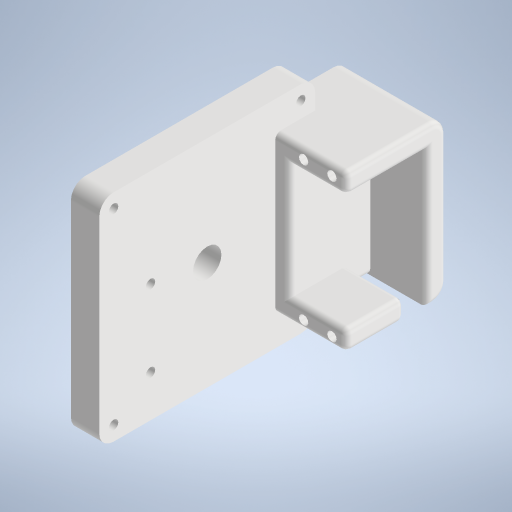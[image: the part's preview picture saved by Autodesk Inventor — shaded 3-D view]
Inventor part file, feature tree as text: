
AUTODESK INVENTOR PART (.ipt)
format: ipt  version: 2023 (Build 270158000, 158)  size: 377,344 bytes
history: native  units: in
note: dims shown in document units (in); Inventor stores cm internally (conversion verified against a paired STEP export)
features: extrude x9, sketch x7, fillet x5
ambient origin geometry x8: Origin, YZ Plane, XZ Plane, XY Plane, X Axis, Y Axis, Z Axis, Center Point
bodies: Solid1 (feature_tree)
feature tree (21):
  extrude  "Extrusion1"  Depth=2.1654in
  sketch  "Sketch2"  dims[d9=0.3937in d10=0.0in d11=0.2756in]
  extrude  "Extrusion2"  Depth=0.2756in
  extrude  "Extrusion3"  Depth=0.2756in
  extrude  "Extrusion5"  Depth=0.2756in
  extrude  "Extrusion6"  Depth=0.1969in TaperAngle=0.0deg
  fillet  "Fillet2"  Radius=0.1969in
  sketch  "Sketch8"  dims[d16=0.9843in d17=0.0in d18=0.1969in d19=0.0in d25=0.1969in d26=0.0in]
  extrude  "Extrusion8"  Depth=0.1969in
  extrude  "Extrusion9"  Depth=0.1969in
  fillet  "Fillet3"  Radius=0.1575in
  fillet  "Fillet4"  Radius=0.3937in
  fillet  "Fillet5"  Radius=0.3937in
  extrude  "Extrusion10"  Depth=0.1969in
  extrude  "Extrusion11"  Depth=0.1969in
  fillet  "Fillet6"  Radius=0.3937in
  sketch  "Sketch1"  dims[d0=3.3268in d1=2.1654in]
  sketch  "Sketch4"  dims[d12=1.122in d13=0.2756in]
  sketch  "Sketch5"  dims[d14=1.122in d15=0.2756in]
  sketch  "Sketch9"  dims[d27=0.315in d29=0.1969in]
  sketch  "Sketch10"  dims[d30=0.1575in d31=0.1299in d32=0.1575in d34=0.3937in d35=0.3937in d36=0.0in d54=0.1969in d55=0.8268in d56=0.3937in d57=0.0787in d58=0.0in d59=0.0in d60=0.0in d61=0.0787in d62=0.0787in d63=0.0787in d64=1.063in d65=0.1299in d66=0.1575in d67=0.1969in d68=0.0in d69=0.0in d70=0.9843in d71=1.0827in d72=3.0in d73=3.0in d74=0.1299in d75=0.2in d76=0.3937in d77=0.0in d78=0.1969in d86=0.9055in]
